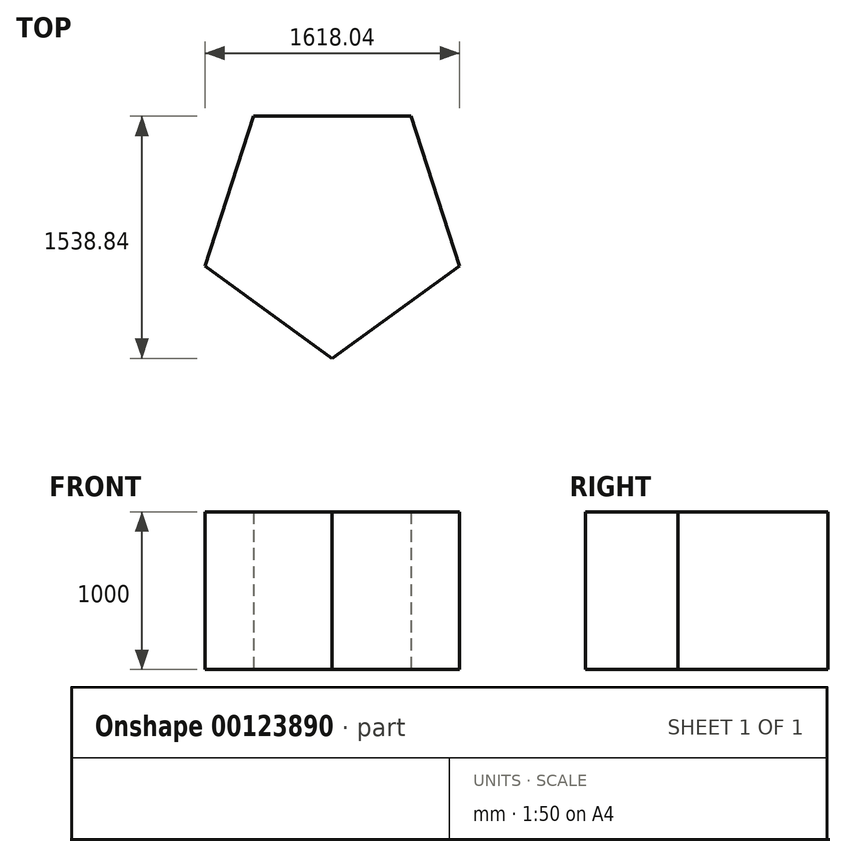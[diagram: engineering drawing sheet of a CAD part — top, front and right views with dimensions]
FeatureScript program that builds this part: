
annotation { "Feature Type Name" : "Feature", "Feature Type Description" : "" }
export const myFeature = defineFeature(function(context is Context, id is Id, definition is map)
    precondition{}
    {
        {
            var Q0;
            Q0=qCreatedBy(makeId("Top.planeOp"),FACE);
            var sketch = newSketch(context, id + "F0", { "sketchPlane" : qUnion([Q0])});
            skCircle(sketch, "E0.cCircle", {"center": v(0, 0) * mm, "radius": 688.2 * mm, "construction": true});
            skLineSegment(sketch, "E0.0", {"start": v(-500, 688.2) * mm, "end": v(500, 688.2) * mm});
            skLineSegment(sketch, "E0.1", {"start": v(500, 688.2) * mm, "end": v(809.02, -262.87) * mm});
            skLineSegment(sketch, "E0.2", {"start": v(809.02, -262.87) * mm, "end": v(0, -850.65) * mm});
            skLineSegment(sketch, "E0.3", {"start": v(0, -850.65) * mm, "end": v(-809.02, -262.87) * mm});
            skLineSegment(sketch, "E0.4", {"start": v(-809.02, -262.87) * mm, "end": v(-500, 688.2) * mm});
            skPoint(sketch, "E0.0.midPoint", {"position": v(0, 688.2) * mm});
            skSolve(sketch);
        }
        {
            var Q0;
            Q0=makeQuery(id+"F0.imprint","IMPRINT",FACE,{"disambiguationData":[TD([[makeQuery(id+"F0.imprint","IMPRINT",EDGE,{"derivedFrom":sQuery(id+"F0.wireOp",EDGE,"E0.0")}),-1.0]])]});
            extrude(context, id + "F1", {"entities" : qUnion([Q0]), "depth" : 1000 * mm});
        }
    });
